# Revit family: Bath-Freestanding-KOHLER-ARTIFACTS-K-21000T_1
name_source: partatom
category: Plumbing Fixtures
revit_build: Autodesk Revit 2017 (Build: 20160225_1515(x64)
units: mm (PartAtom-declared; Revit-internal decimal feet)

## family parameters
Cut with Voids When Loaded = No
Host = Face
OmniClass Number = 23.31.15.00
OmniClass Title = Bathtubs
Part Type = Normal
Room Calculation Point = No
Round Connector Dimension = Use Diameter
Shared = No

## types (2) — shared parameters
ADA Compliant = No
Assembly Code = D2010500
CW Connection = No
Cold Water Inlet = Cold Water Inlet
Date Modified = 01/14/2021
Default Elevation = 0"
Drain Included = No
Finish = KOHLER-Cast_Iron-0-White
HW Connection = No
Height = 27 7/8"
Height1 = 15/16"
Hot Water Inlet = Hot Water Inlet
Legs = Yes
Legs Included = No
Length = 66 1/8"
Manufacturer = KOHLER Co.
MasterFormat 1995 = 15410
MasterFormat 2004 = 22.41.19
Material = Enameled Cast Iron
Product Documentation Link = https://files.kohler.com.cn
Product Name = ARTIFACTS
Product Page URL = https://www.kohler.com.cn
Vent Connection = No
Waste Connection = Yes
Waste Water Outlet = Waste Water Outlet
WaterSense Certified = No
Width = 32 1/2"

## per-type parameters (varying)
| type | Description | Legs Material | Model | Outerside Material | Type | URL |
| White Exterior,0-White, White Legs | Artisi freestanding cast iron bathtub (white outside) | KOHLER-Cast_Iron-0-White | K-21000T-0 | KOHLER-Cast_Iron-0-White | 1 | http://www.kohler.com.cn |
| Black Exterior,0-White, Iron Black Legs | Artisi freestanding cast iron bathtub (black outside) | KOHLER-Cast_Iron-P5-Iron_Black | K-21000T-P5-0 | KOHLER-Enameled_Cast_Iron-7-Black_Black | 2 | https://www.us.kohler.com |

## geometry (parser evidence)
native form markers: Sweep x6
no freeform markers — native parametric forms only
